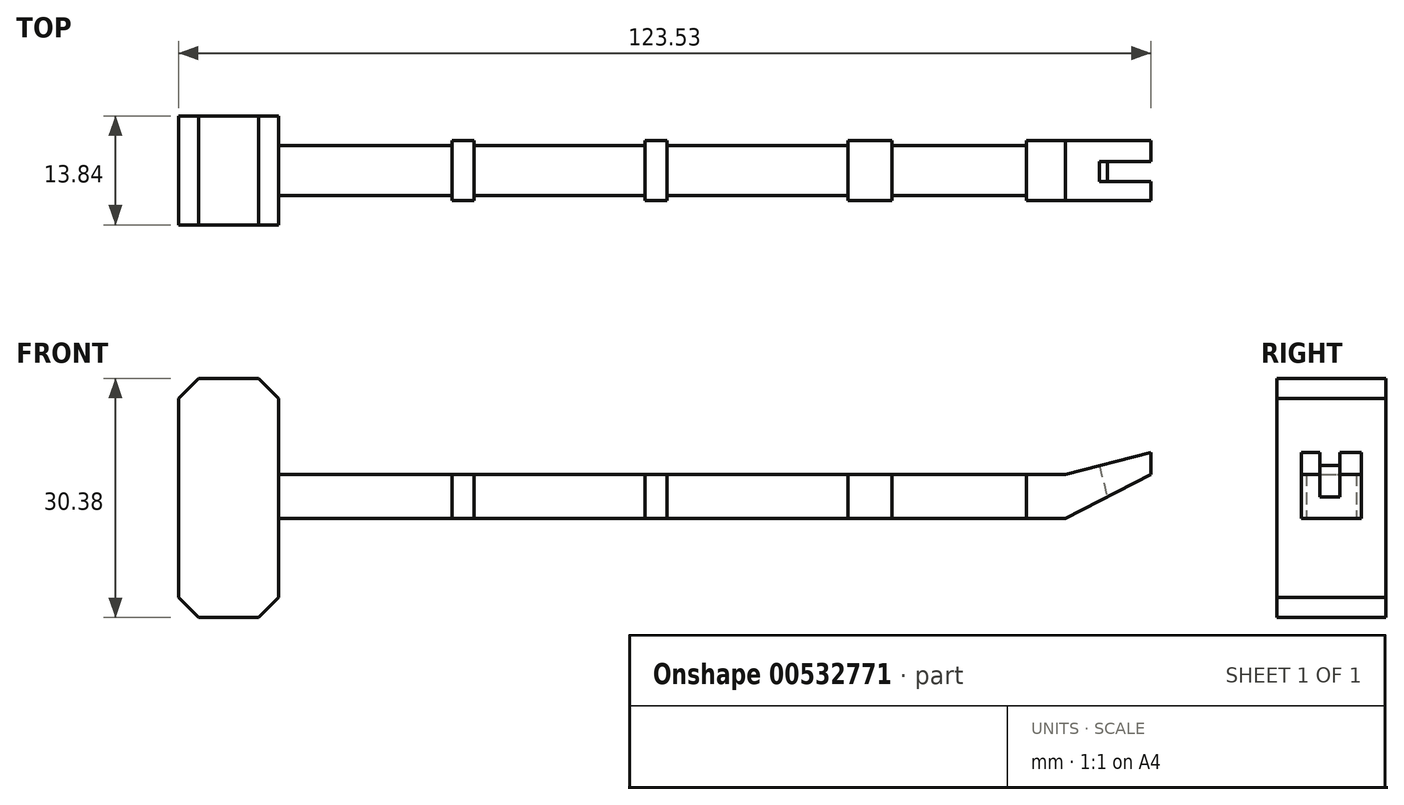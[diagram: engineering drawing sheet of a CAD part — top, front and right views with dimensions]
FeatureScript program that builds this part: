
annotation { "Feature Type Name" : "Feature", "Feature Type Description" : "" }
export const myFeature = defineFeature(function(context is Context, id is Id, definition is map)
    precondition{}
    {
        {
            var Q0;
            Q0=qCreatedBy(makeId("Front.planeOp"),FACE);
            var sketch = newSketch(context, id + "F0", { "sketchPlane" : qUnion([Q0])});
            skLineSegment(sketch, "E0", {"start": v(-49.36, 33.84) * mm, "end": v(48.43, 33.84) * mm});
            skLineSegment(sketch, "E1", {"start": v(48.43, 33.84) * mm, "end": v(48.43, 28.25) * mm});
            skLineSegment(sketch, "E2", {"start": v(48.43, 28.25) * mm, "end": v(-49.36, 28.25) * mm});
            skLineSegment(sketch, "E3", {"start": v(48.43, 33.84) * mm, "end": v(53.4, 33.84) * mm});
            skLineSegment(sketch, "E4", {"start": v(53.4, 33.84) * mm, "end": v(64.26, 36.63) * mm});
            skLineSegment(sketch, "E5", {"start": v(64.26, 36.63) * mm, "end": v(64.26, 33.84) * mm});
            skLineSegment(sketch, "E6", {"start": v(64.26, 33.84) * mm, "end": v(53.4, 28.25) * mm});
            skLineSegment(sketch, "E7", {"start": v(53.4, 28.25) * mm, "end": v(48.43, 28.25) * mm});
            skLineSegment(sketch, "E8", {"start": v(-46.57, 33.84) * mm, "end": v(-46.57, 28.25) * mm});
            skLineSegment(sketch, "E9", {"start": v(-24.53, 33.84) * mm, "end": v(-24.53, 28.25) * mm});
            skLineSegment(sketch, "E10", {"start": v(-21.73, 33.84) * mm, "end": v(-21.73, 28.25) * mm});
            skLineSegment(sketch, "E11", {"start": v(0, 33.84) * mm, "end": v(0, 28.25) * mm});
            skLineSegment(sketch, "E12", {"start": v(2.8, 33.84) * mm, "end": v(2.8, 28.25) * mm});
            skLineSegment(sketch, "E13", {"start": v(25.77, 33.84) * mm, "end": v(25.77, 28.25) * mm});
            skLineSegment(sketch, "E14", {"start": v(28.56, 33.84) * mm, "end": v(28.56, 28.25) * mm});
            skLineSegment(sketch, "E15", {"start": v(31.35, 33.84) * mm, "end": v(31.35, 28.25) * mm});
            skLineSegment(sketch, "E16", {"start": v(-49.36, 33.84) * mm, "end": v(-49.36, 28.25) * mm});
            skSolve(sketch);
        }
        {
            var Q0;
            {var subQ0=sQuery(id+"F0.wireOp",EDGE,"E8");Q0=makeQuery(id+"F0.imprint","IMPRINT",FACE,{"disambiguationData":[TD([[makeQuery(id+"F0.imprint","IMPRINT",EDGE,{"derivedFrom":subQ0}),1.0]])]});}
            var Q1;
            {var subQ0=sQuery(id+"F0.wireOp",EDGE,"E10");Q1=makeQuery(id+"F0.imprint","IMPRINT",FACE,{"disambiguationData":[TD([[makeQuery(id+"F0.imprint","IMPRINT",EDGE,{"derivedFrom":subQ0}),1.0]])]});}
            var Q2;
            {var subQ0=sQuery(id+"F0.wireOp",EDGE,"E12");Q2=makeQuery(id+"F0.imprint","IMPRINT",FACE,{"disambiguationData":[TD([[makeQuery(id+"F0.imprint","IMPRINT",EDGE,{"derivedFrom":subQ0}),1.0]])]});}
            var Q3;
            {var subQ0=sQuery(id+"F0.wireOp",EDGE,"E1");Q3=makeQuery(id+"F0.imprint","IMPRINT",FACE,{"disambiguationData":[TD([[makeQuery(id+"F0.imprint","IMPRINT",EDGE,{"derivedFrom":subQ0}),-1.0]])]});}
            extrude(context, id + "F1", {"entities" : qUnion([Q0, Q1, Q2, Q3]), "endBound" : BoundingType.SYMMETRIC, "depth" : 6.35 * mm, "offsetDistance" : 25.4 * mm});
        }
        {
            var Q0;
            Q0=makeQuery(id+"F1.opExtrude","SWEPT_FACE",FACE,{"disambiguationData":[OSD([sQuery(id+"F0.wireOp",EDGE,"E8")])]});
            var sketch = newSketch(context, id + "F2", { "sketchPlane" : qUnion([Q0])});
            skLineSegment(sketch, "E17.bottom", {"start": v(-6.92, 46.02) * mm, "end": v(6.92, 46.02) * mm});
            skLineSegment(sketch, "E17.top", {"start": v(-6.92, 15.64) * mm, "end": v(6.92, 15.64) * mm});
            skLineSegment(sketch, "E17.left", {"start": v(-6.92, 46.02) * mm, "end": v(-6.92, 15.64) * mm});
            skLineSegment(sketch, "E17.right", {"start": v(6.92, 46.02) * mm, "end": v(6.92, 15.64) * mm});
            skSolve(sketch);
        }
        {
            var Q0;
            Q0 = qSketchRegion(id + "F2", true);
            extrude(context, id + "F3", {"entities" : qUnion([Q0]), "operationType" : NewBodyOperationType.ADD, "depth" : 12.7 * mm, "offsetDistance" : 25.4 * mm});
        }
        {
            var Q0;
            {var subQ0=sQuery(id+"F0.wireOp",EDGE,"E13");Q0=makeQuery(id+"F0.imprint","IMPRINT",FACE,{"disambiguationData":[TD([[makeQuery(id+"F0.imprint","IMPRINT",EDGE,{"derivedFrom":subQ0}),1.0]])]});}
            var Q1;
            {var subQ0=sQuery(id+"F0.wireOp",EDGE,"E14");Q1=makeQuery(id+"F0.imprint","IMPRINT",FACE,{"disambiguationData":[TD([[makeQuery(id+"F0.imprint","IMPRINT",EDGE,{"derivedFrom":subQ0}),1.0]])]});}
            var Q2;
            Q2=makeQuery(id+"F0.imprint","IMPRINT",FACE,{"disambiguationData":[TD([[makeQuery(id+"F0.imprint","IMPRINT",EDGE,{"derivedFrom":sQuery(id+"F0.wireOp",EDGE,"E1")}),1.0]])]});
            var Q3;
            {var subQ0=sQuery(id+"F0.wireOp",EDGE,"E9");Q3=makeQuery(id+"F0.imprint","IMPRINT",FACE,{"disambiguationData":[TD([[makeQuery(id+"F0.imprint","IMPRINT",EDGE,{"derivedFrom":subQ0}),1.0]])]});}
            var Q4;
            {var subQ0=sQuery(id+"F0.wireOp",EDGE,"E11");Q4=makeQuery(id+"F0.imprint","IMPRINT",FACE,{"disambiguationData":[TD([[makeQuery(id+"F0.imprint","IMPRINT",EDGE,{"derivedFrom":subQ0}),1.0]])]});}
            extrude(context, id + "F4", {"entities" : qUnion([Q0, Q1, Q2, Q3, Q4]), "endBound" : BoundingType.SYMMETRIC, "depth" : 7.62 * mm, "offsetDistance" : 25.4 * mm});
        }
        {
            var Q0;
            Q0=makeQuery(id+"F4.opExtrude","SWEPT_FACE",FACE,{"disambiguationData":[OSD([sQuery(id+"F0.wireOp",EDGE,"E4")])]});
            var sketch = newSketch(context, id + "F5", { "sketchPlane" : qUnion([Q0])});
            skLineSegment(sketch, "E18.bottom", {"start": v(64.58, -1.44) * mm, "end": v(71.36, -1.44) * mm});
            skLineSegment(sketch, "E18.top", {"start": v(64.58, 1.11) * mm, "end": v(71.36, 1.11) * mm});
            skLineSegment(sketch, "E18.left", {"start": v(64.58, -1.44) * mm, "end": v(64.58, 1.11) * mm});
            skLineSegment(sketch, "E18.right", {"start": v(71.36, -1.44) * mm, "end": v(71.36, 1.11) * mm});
            skSolve(sketch);
        }
        {
            var Q0;
            Q0 = qSketchRegion(id + "F5", true);
            extrude(context, id + "F6", {"entities" : qUnion([Q0]), "operationType" : NewBodyOperationType.REMOVE, "endBound" : BoundingType.SYMMETRIC, "depth" : 25.4 * mm, "offsetDistance" : 25.4 * mm});
        }
        {
            var Q0;
            Q0=makeQuery(id+"F3.opExtrude","CAP_EDGE",EDGE,{"disambiguationData":[OSD([sQuery(id+"F2.wireOp",EDGE,"E17.bottom")])],"isStart":false});
            var Q1;
            Q1=makeQuery(id+"F3.opExtrude","CAP_EDGE",EDGE,{"disambiguationData":[OSD([sQuery(id+"F2.wireOp",EDGE,"E17.top")])],"isStart":false});
            var Q2;
            Q2=makeQuery(id+"F3.opExtrude","CAP_EDGE",EDGE,{"disambiguationData":[OSD([sQuery(id+"F2.wireOp",EDGE,"E17.top")])],"isStart":true});
            var Q3;
            Q3=makeQuery(id+"F3.opExtrude","CAP_EDGE",EDGE,{"disambiguationData":[OSD([sQuery(id+"F2.wireOp",EDGE,"E17.bottom")])],"isStart":true});
            chamfer(context, id + "F7", {"entities" : qUnion([Q0, Q1, Q2, Q3]), "width" : 2.54 * mm, "tangentPropagation" : true});
        }
    });
